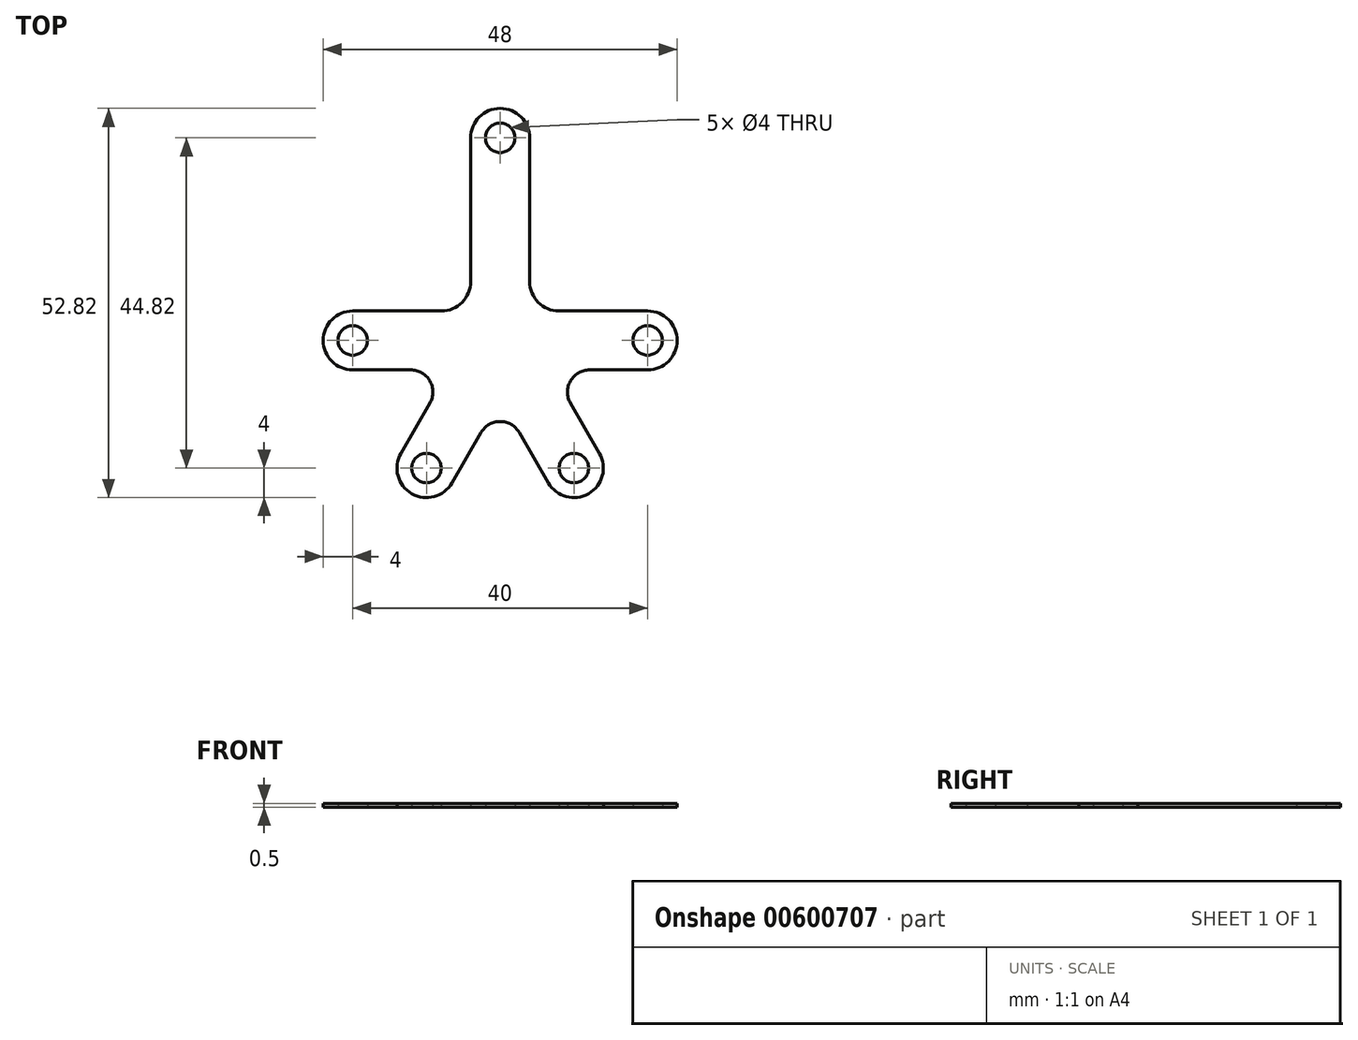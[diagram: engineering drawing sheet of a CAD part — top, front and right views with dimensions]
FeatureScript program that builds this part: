
annotation { "Feature Type Name" : "Feature", "Feature Type Description" : "" }
export const myFeature = defineFeature(function(context is Context, id is Id, definition is map)
    precondition{}
    {
        {
            var Q0;
            Q0=qCreatedBy(makeId("Top.planeOp"),FACE);
            var sketch = newSketch(context, id + "F0", { "sketchPlane" : qUnion([Q0])});
            skCircle(sketch, "E0", {"center": v(-20, 0) * mm, "radius": 2 * mm});
            skCircle(sketch, "E1", {"center": v(20, 0) * mm, "radius": 2 * mm});
            skCircle(sketch, "E2", {"center": v(0, 27.5) * mm, "radius": 2 * mm});
            skCircle(sketch, "E3", {"center": v(-10, -17.32) * mm, "radius": 2 * mm});
            skCircle(sketch, "E4", {"center": v(10, -17.32) * mm, "radius": 2 * mm});
            skLineSegment(sketch, "E5", {"start": v(-20, 0) * mm, "end": v(-10, -17.32) * mm});
            skLineSegment(sketch, "E6", {"start": v(-10, -17.32) * mm, "end": v(10, -17.32) * mm});
            skLineSegment(sketch, "E7", {"start": v(10, -17.32) * mm, "end": v(20, 0) * mm});
            skLineSegment(sketch, "E8", {"start": v(-10, -17.32) * mm, "end": v(0, 0) * mm});
            skLineSegment(sketch, "E9", {"start": v(-20, 0) * mm, "end": v(0, 0) * mm});
            skCircle(sketch, "E10", {"center": v(-20, 0) * mm, "radius": 4 * mm});
            skCircle(sketch, "E11", {"center": v(-10, -17.32) * mm, "radius": 4 * mm});
            skCircle(sketch, "E12", {"center": v(10, -17.32) * mm, "radius": 4 * mm});
            skCircle(sketch, "E13", {"center": v(20, 0) * mm, "radius": 4 * mm});
            skCircle(sketch, "E14", {"center": v(0, 27.5) * mm, "radius": 4 * mm});
            skLineSegment(sketch, "E15", {"start": v(-20, 4) * mm, "end": v(-8, 4) * mm});
            skLineSegment(sketch, "E16", {"start": v(-4, 8) * mm, "end": v(-4, 27.5) * mm});
            skLineSegment(sketch, "E17", {"start": v(-20, -4) * mm, "end": v(-12.12, -4) * mm});
            skLineSegment(sketch, "E18", {"start": v(-9.53, -8.5) * mm, "end": v(-13.46, -15.32) * mm});
            skLineSegment(sketch, "E19", {"start": v(-6.54, -19.32) * mm, "end": v(-2.6, -12.5) * mm});
            skPoint(sketch, "E19.endSnap0", {"position": v(-5, -8.66) * mm});
            skLineSegment(sketch, "E20", {"start": v(2.6, -12.5) * mm, "end": v(6.54, -19.32) * mm});
            skLineSegment(sketch, "E21", {"start": v(13.46, -15.32) * mm, "end": v(9.53, -8.5) * mm});
            skLineSegment(sketch, "E22", {"start": v(12.12, -4) * mm, "end": v(20, -4) * mm});
            skLineSegment(sketch, "E23", {"start": v(20, 4) * mm, "end": v(8, 4) * mm});
            skLineSegment(sketch, "E24", {"start": v(4, 8) * mm, "end": v(4, 27.5) * mm});
            skLineSegment(sketch, "E25", {"start": v(10, -17.32) * mm, "end": v(0, 0) * mm});
            skPoint(sketch, "E26.visualSharp", {"position": v(-4, 4) * mm});
            skArc(sketch, "E26.filletArc", {"start": v(-8, 4) * mm, "mid": v(-5.17, 5.17) * mm, "end": v(-4, 8) * mm});
            skPoint(sketch, "E27.visualSharp", {"position": v(4, 4) * mm});
            skArc(sketch, "E27.filletArc", {"start": v(4, 8) * mm, "mid": v(5.17, 5.17) * mm, "end": v(8, 4) * mm});
            skPoint(sketch, "E28.visualSharp", {"position": v(6.93, -4) * mm});
            skArc(sketch, "E28.filletArc", {"start": v(12.12, -4) * mm, "mid": v(9.53, -5.5) * mm, "end": v(9.53, -8.5) * mm});
            skPoint(sketch, "E29.visualSharp", {"position": v(-6.93, -4) * mm});
            skArc(sketch, "E29.filletArc", {"start": v(-9.53, -8.5) * mm, "mid": v(-9.53, -5.5) * mm, "end": v(-12.12, -4) * mm});
            skPoint(sketch, "E30.visualSharp", {"position": v(0, -8) * mm});
            skArc(sketch, "E30.filletArc", {"start": v(2.6, -12.5) * mm, "mid": v(0, -11) * mm, "end": v(-2.6, -12.5) * mm});
            skSolve(sketch);
        }
        {
            var Q0;
            {var subQ6=sQuery(id+"F0.wireOp",EDGE,"E15");Q0=makeQuery(id+"F0.imprint","IMPRINT",FACE,{"disambiguationData":[TD([[makeQuery(id+"F0.imprint","IMPRINT",EDGE,{"derivedFrom":subQ6}),-1.0]])]});}
            var Q1;
            {var subQ7=sQuery(id+"F0.wireOp",EDGE,"E17");var subQ8=sQuery(id+"F0.wireOp",EDGE,"E5");var subQ9=makeQuery(id+"F0.imprint","INTERSECT",VERTEX,{"derivedFrom":[subQ8,subQ7]});Q1=makeQuery(id+"F0.imprint","IMPRINT",FACE,{"disambiguationData":[TD([[makeQuery(id+"F0.imprint","IMPRINT",EDGE,{"disambiguationData":[TD([[subQ9,1.0]])],"derivedFrom":subQ8}),1.0]])]});}
            var Q2;
            {var subQ6=sQuery(id+"F0.wireOp",EDGE,"E6");var subQ11=sQuery(id+"F0.wireOp",EDGE,"E19");var subQ13=makeQuery(id+"F0.imprint","INTERSECT",VERTEX,{"derivedFrom":[subQ6,subQ11]});Q2=makeQuery(id+"F0.imprint","IMPRINT",FACE,{"disambiguationData":[TD([[makeQuery(id+"F0.imprint","IMPRINT",EDGE,{"disambiguationData":[TD([[subQ13,1.0]])],"derivedFrom":subQ6}),1.0]])]});}
            var Q3;
            {var subQ0=sQuery(id+"F0.wireOp",EDGE,"E8");var subQ1=sQuery(id+"F0.wireOp",EDGE,"E3");var subQ2=makeQuery(id+"F0.imprint","INTERSECT",VERTEX,{"derivedFrom":[subQ1,subQ0]});Q3=makeQuery(id+"F0.imprint","IMPRINT",FACE,{"disambiguationData":[TD([[makeQuery(id+"F0.imprint","IMPRINT",EDGE,{"disambiguationData":[TD([[subQ2,-1.0]])],"derivedFrom":subQ1}),-1.0]])]});}
            var Q4;
            {var subQ0=sQuery(id+"F0.wireOp",EDGE,"E6");var subQ1=sQuery(id+"F0.wireOp",EDGE,"E3");var subQ2=makeQuery(id+"F0.imprint","INTERSECT",VERTEX,{"derivedFrom":[subQ1,subQ0]});Q4=makeQuery(id+"F0.imprint","IMPRINT",FACE,{"disambiguationData":[TD([[makeQuery(id+"F0.imprint","IMPRINT",EDGE,{"disambiguationData":[TD([[subQ2,1.0]])],"derivedFrom":subQ1}),-1.0]])]});}
            var Q5;
            {var subQ0=sQuery(id+"F0.wireOp",EDGE,"E8");var subQ1=sQuery(id+"F0.wireOp",EDGE,"E3");var subQ2=makeQuery(id+"F0.imprint","INTERSECT",VERTEX,{"derivedFrom":[subQ1,subQ0]});Q5=makeQuery(id+"F0.imprint","IMPRINT",FACE,{"disambiguationData":[TD([[makeQuery(id+"F0.imprint","IMPRINT",EDGE,{"disambiguationData":[TD([[subQ2,1.0]])],"derivedFrom":subQ1}),-1.0]])]});}
            var Q6;
            {var subQ0=sQuery(id+"F0.wireOp",EDGE,"E7");var subQ1=sQuery(id+"F0.wireOp",EDGE,"E4");var subQ2=makeQuery(id+"F0.imprint","INTERSECT",VERTEX,{"derivedFrom":[subQ1,subQ0]});Q6=makeQuery(id+"F0.imprint","IMPRINT",FACE,{"disambiguationData":[TD([[makeQuery(id+"F0.imprint","IMPRINT",EDGE,{"disambiguationData":[TD([[subQ2,1.0]])],"derivedFrom":subQ1}),-1.0]])]});}
            var Q7;
            {var subQ0=sQuery(id+"F0.wireOp",EDGE,"E25");var subQ1=sQuery(id+"F0.wireOp",EDGE,"E4");var subQ2=makeQuery(id+"F0.imprint","INTERSECT",VERTEX,{"derivedFrom":[subQ1,subQ0]});Q7=makeQuery(id+"F0.imprint","IMPRINT",FACE,{"disambiguationData":[TD([[makeQuery(id+"F0.imprint","IMPRINT",EDGE,{"disambiguationData":[TD([[subQ2,-1.0]])],"derivedFrom":subQ1}),-1.0]])]});}
            var Q8;
            {var subQ0=sQuery(id+"F0.wireOp",EDGE,"E25");var subQ1=sQuery(id+"F0.wireOp",EDGE,"E4");var subQ2=makeQuery(id+"F0.imprint","INTERSECT",VERTEX,{"derivedFrom":[subQ1,subQ0]});Q8=makeQuery(id+"F0.imprint","IMPRINT",FACE,{"disambiguationData":[TD([[makeQuery(id+"F0.imprint","IMPRINT",EDGE,{"disambiguationData":[TD([[subQ2,1.0]])],"derivedFrom":subQ1}),-1.0]])]});}
            var Q9;
            {var subQ1=sQuery(id+"F0.wireOp",EDGE,"E0");var subQ5=sQuery(id+"F0.wireOp",EDGE,"E5");var subQ6=makeQuery(id+"F0.imprint","INTERSECT",VERTEX,{"derivedFrom":[subQ1,subQ5]});Q9=makeQuery(id+"F0.imprint","IMPRINT",FACE,{"disambiguationData":[TD([[makeQuery(id+"F0.imprint","IMPRINT",EDGE,{"disambiguationData":[TD([[subQ6,1.0]])],"derivedFrom":subQ1}),-1.0]])]});}
            var Q10;
            {var subQ0=sQuery(id+"F0.wireOp",EDGE,"E5");var subQ1=sQuery(id+"F0.wireOp",EDGE,"E0");var subQ2=makeQuery(id+"F0.imprint","INTERSECT",VERTEX,{"derivedFrom":[subQ1,subQ0]});Q10=makeQuery(id+"F0.imprint","IMPRINT",FACE,{"disambiguationData":[TD([[makeQuery(id+"F0.imprint","IMPRINT",EDGE,{"disambiguationData":[TD([[subQ2,-1.0]])],"derivedFrom":subQ1}),-1.0]])]});}
            var Q11;
            Q11=makeQuery(id+"F0.imprint","IMPRINT",FACE,{"disambiguationData":[TD([[makeQuery(id+"F0.imprint","IMPRINT",EDGE,{"derivedFrom":sQuery(id+"F0.wireOp",EDGE,"E1")}),-1.0]])]});
            var Q12;
            Q12=makeQuery(id+"F0.imprint","IMPRINT",FACE,{"disambiguationData":[TD([[makeQuery(id+"F0.imprint","IMPRINT",EDGE,{"derivedFrom":sQuery(id+"F0.wireOp",EDGE,"E2")}),-1.0]])]});
            var Q13;
            {var subQ0=sQuery(id+"F0.wireOp",EDGE,"E17");var subQ1=sQuery(id+"F0.wireOp",EDGE,"E5");var subQ2=makeQuery(id+"F0.imprint","INTERSECT",VERTEX,{"derivedFrom":[subQ1,subQ0]});Q13=makeQuery(id+"F0.imprint","IMPRINT",FACE,{"disambiguationData":[TD([[makeQuery(id+"F0.imprint","IMPRINT",EDGE,{"disambiguationData":[TD([[subQ2,1.0]])],"derivedFrom":subQ1}),-1.0]])]});}
            var Q14;
            {var subQ0=sQuery(id+"F0.wireOp",EDGE,"E18");var subQ1=sQuery(id+"F0.wireOp",EDGE,"E5");var subQ2=makeQuery(id+"F0.imprint","INTERSECT",VERTEX,{"derivedFrom":[subQ1,subQ0]});Q14=makeQuery(id+"F0.imprint","IMPRINT",FACE,{"disambiguationData":[TD([[makeQuery(id+"F0.imprint","IMPRINT",EDGE,{"disambiguationData":[TD([[subQ2,-1.0]])],"derivedFrom":subQ1}),-1.0]])]});}
            var Q15;
            {var subQ0=sQuery(id+"F0.wireOp",EDGE,"E19");var subQ1=sQuery(id+"F0.wireOp",EDGE,"E6");var subQ2=makeQuery(id+"F0.imprint","INTERSECT",VERTEX,{"derivedFrom":[subQ1,subQ0]});Q15=makeQuery(id+"F0.imprint","IMPRINT",FACE,{"disambiguationData":[TD([[makeQuery(id+"F0.imprint","IMPRINT",EDGE,{"disambiguationData":[TD([[subQ2,1.0]])],"derivedFrom":subQ1}),-1.0]])]});}
            var Q16;
            {var subQ0=sQuery(id+"F0.wireOp",EDGE,"E20");var subQ1=sQuery(id+"F0.wireOp",EDGE,"E6");var subQ2=makeQuery(id+"F0.imprint","INTERSECT",VERTEX,{"derivedFrom":[subQ1,subQ0]});Q16=makeQuery(id+"F0.imprint","IMPRINT",FACE,{"disambiguationData":[TD([[makeQuery(id+"F0.imprint","IMPRINT",EDGE,{"disambiguationData":[TD([[subQ2,-1.0]])],"derivedFrom":subQ1}),-1.0]])]});}
            var Q17;
            {var subQ0=sQuery(id+"F0.wireOp",EDGE,"E21");var subQ1=sQuery(id+"F0.wireOp",EDGE,"E7");var subQ2=makeQuery(id+"F0.imprint","INTERSECT",VERTEX,{"derivedFrom":[subQ1,subQ0]});Q17=makeQuery(id+"F0.imprint","IMPRINT",FACE,{"disambiguationData":[TD([[makeQuery(id+"F0.imprint","IMPRINT",EDGE,{"disambiguationData":[TD([[subQ2,1.0]])],"derivedFrom":subQ1}),-1.0]])]});}
            var Q18;
            {var subQ0=sQuery(id+"F0.wireOp",EDGE,"E22");var subQ1=sQuery(id+"F0.wireOp",EDGE,"E7");var subQ2=makeQuery(id+"F0.imprint","INTERSECT",VERTEX,{"derivedFrom":[subQ1,subQ0]});Q18=makeQuery(id+"F0.imprint","IMPRINT",FACE,{"disambiguationData":[TD([[makeQuery(id+"F0.imprint","IMPRINT",EDGE,{"disambiguationData":[TD([[subQ2,-1.0]])],"derivedFrom":subQ1}),-1.0]])]});}
            extrude(context, id + "F1", {"entities" : qUnion([Q0, Q1, Q2, Q3, Q4, Q5, Q6, Q7, Q8, Q9, Q10, Q11, Q12, Q13, Q14, Q15, Q16, Q17, Q18]), "flatOperationType" : FlatOperationType.REMOVE, "depth" : 0.5 * mm, "offsetDistance" : 25 * mm, "domain" : OperationDomain.MODEL});
        }
    });
